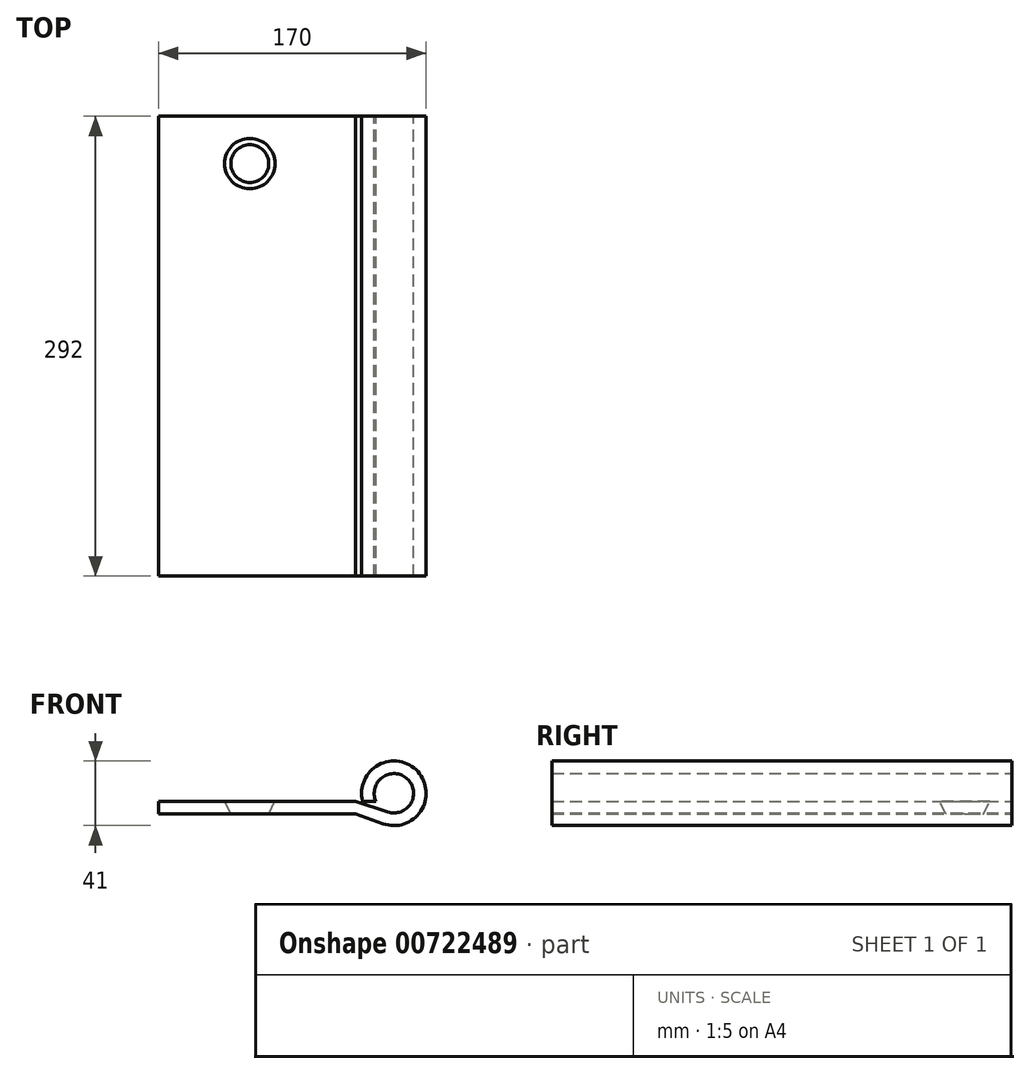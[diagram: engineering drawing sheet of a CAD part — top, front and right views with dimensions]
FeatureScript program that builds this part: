
annotation { "Feature Type Name" : "Feature", "Feature Type Description" : "" }
export const myFeature = defineFeature(function(context is Context, id is Id, definition is map)
    precondition{}
    {
        {
            var Q0;
            Q0=qCreatedBy(makeId("Front.planeOp"),FACE);
            var sketch = newSketch(context, id + "F0", { "sketchPlane" : qUnion([Q0])});
            skLineSegment(sketch, "E0", {"start": v(0, 0) * mm, "end": v(-125, 0) * mm});
            skLineSegment(sketch, "E1", {"start": v(-125, 0) * mm, "end": v(-125, -8) * mm});
            skLineSegment(sketch, "E2", {"start": v(-125, -8) * mm, "end": v(0, -8) * mm});
            skArc(sketch, "E3", {"start": v(20.54, -6.86) * mm, "mid": v(32.94, 14.22) * mm, "end": v(13.04, 0) * mm});
            skArc(sketch, "E4", {"start": v(17.59, -14.3) * mm, "mid": v(39.69, 18.77) * mm, "end": v(4.62, 0) * mm});
            skLineSegment(sketch, "E5", {"start": v(4.62, 0) * mm, "end": v(13.04, 0) * mm});
            skLineSegment(sketch, "E6", {"start": v(0, 0) * mm, "end": v(20.54, -6.86) * mm});
            skLineSegment(sketch, "E7", {"start": v(0, -8) * mm, "end": v(17.59, -14.3) * mm});
            skSolve(sketch);
        }
        {
            var Q0;
            Q0 = qSketchRegion(id + "F0", true);
            extrude(context, id + "F1", {"entities" : qUnion([Q0]), "depth" : 292 * mm, "offsetDistance" : 25 * mm});
        }
        {
            var Q0;
            Q0=makeQuery(id+"F1.opExtrude","SWEPT_FACE",FACE,{"disambiguationData":[OSD([sQuery(id+"F0.wireOp",EDGE,"E0")])]});
            var sketch = newSketch(context, id + "F2", { "sketchPlane" : qUnion([Q0])});
            skLineSegment(sketch, "E8", {"start": v(-125, -146) * mm, "end": v(98.58, -146) * mm, "construction": true});
            skCircle(sketch, "E9", {"center": v(-67, -30) * mm, "radius": 16 * mm});
            skCircle(sketch, "E10", {"center": v(-95, -146) * mm, "radius": 16 * mm});
            skCircle(sketch, "E11.MirrorC", {"center": v(-67, -262) * mm, "radius": 16 * mm});
            skSolve(sketch);
        }
        {
            var Q0;
            Q0=makeQuery(id+"F1.opExtrude","SWEPT_FACE",FACE,{"disambiguationData":[OSD([sQuery(id+"F0.wireOp",EDGE,"E2")])]});
            var sketch = newSketch(context, id + "F3", { "sketchPlane" : qUnion([Q0])});
            skPoint(sketch, "E12.0", {"position": v(-67, 30) * mm});
            skPoint(sketch, "E13.0", {"position": v(-95, 146) * mm});
            skPoint(sketch, "E14.0", {"position": v(-67, 262) * mm});
            skCircle(sketch, "E15", {"center": v(-67, 30) * mm, "radius": 12 * mm});
            skCircle(sketch, "E16", {"center": v(-95, 146) * mm, "radius": 12 * mm});
            skCircle(sketch, "E17", {"center": v(-67, 262) * mm, "radius": 12 * mm});
            skSolve(sketch);
        }
        {
            var Q1;
            Q1=makeQuery(id+"F3.imprint","IMPRINT",FACE,{"disambiguationData":[TD([[makeQuery(id+"F3.imprint","IMPRINT",EDGE,{"derivedFrom":sQuery(id+"F3.wireOp",EDGE,"E15")}),1.0]])]});
            var Q2;
            Q2=makeQuery(id+"F2.imprint","IMPRINT",FACE,{"disambiguationData":[TD([[makeQuery(id+"F2.imprint","IMPRINT",EDGE,{"derivedFrom":sQuery(id+"F2.wireOp",EDGE,"E9")}),1.0]])]});
            loft(context, id + "F4", {"operationType" : NewBodyOperationType.REMOVE, "sheetProfilesArray" : [{ "sheetProfileEntities" : qUnion([Q1]) }, { "sheetProfileEntities" : qUnion([Q2]) }]});
        }
    });
